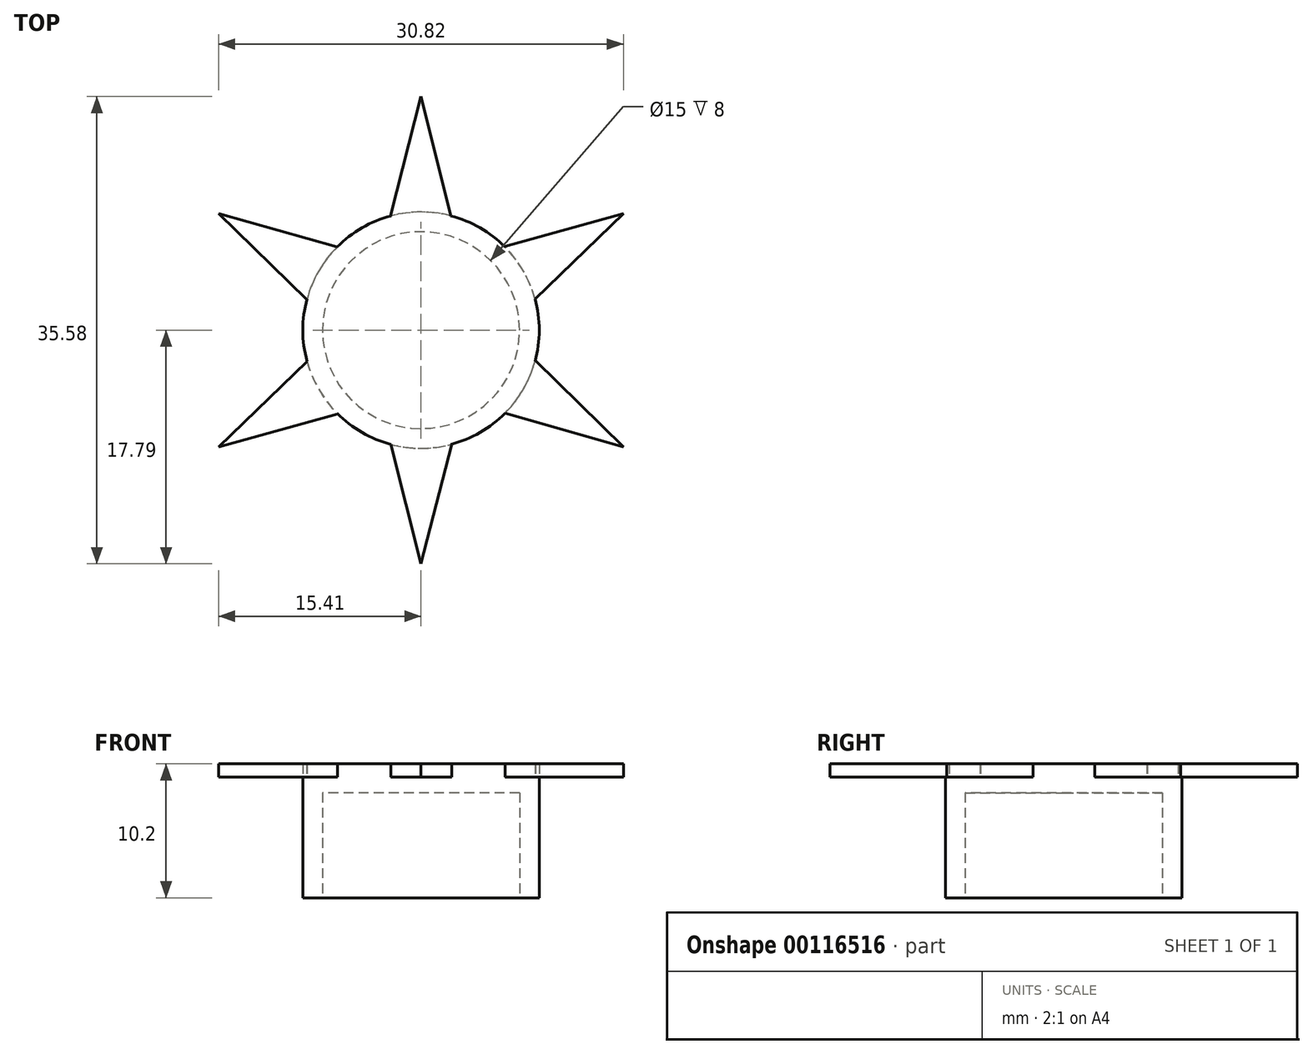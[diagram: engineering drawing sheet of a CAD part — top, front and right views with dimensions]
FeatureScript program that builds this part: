
annotation { "Feature Type Name" : "Feature", "Feature Type Description" : "" }
export const myFeature = defineFeature(function(context is Context, id is Id, definition is map)
    precondition{}
    {
        {
            var Q0;
            Q0=qCreatedBy(makeId("Top.planeOp"),FACE);
            var sketch = newSketch(context, id + "F0", { "sketchPlane" : qUnion([Q0])});
            skCircle(sketch, "E0", {"center": v(0, 0) * mm, "radius": 7.5 * mm});
            skCircle(sketch, "E1", {"center": v(0, 0) * mm, "radius": 9 * mm});
            skSolve(sketch);
        }
        {
            var Q0;
            Q0 = qSketchRegion(id + "F0", true);
            extrude(context, id + "F1", {"entities" : qUnion([Q0]), "depth" : 8 * mm});
        }
        {
            var Q0;
            Q0=makeQuery(id+"F1.opExtrude","CAP_FACE",FACE,{"disambiguationData":[OSD([sQuery(id+"F0.wireOp",EDGE,"E0"),sQuery(id+"F0.wireOp",EDGE,"E1")])],"isStart":false});
            var sketch = newSketch(context, id + "F2", { "sketchPlane" : qUnion([Q0])});
            skCircle(sketch, "E2.0", {"center": v(0, 0) * mm, "radius": 9 * mm});
            skSolve(sketch);
        }
        {
            var Q0;
            Q0 = qSketchRegion(id + "F2", true);
            extrude(context, id + "F3", {"entities" : qUnion([Q0]), "operationType" : NewBodyOperationType.ADD, "depth" : 1.2 * mm});
        }
        {
            var Q0;
            Q0=makeQuery(id+"F3.opExtrude","CAP_FACE",FACE,{"disambiguationData":[OSD([sQuery(id+"F2.wireOp",EDGE,"E2.0")])],"isStart":false});
            var sketch = newSketch(context, id + "F4", { "sketchPlane" : qUnion([Q0])});
            skLineSegment(sketch, "E3", {"start": v(-2.34, 8.7) * mm, "end": v(0, 17.8) * mm});
            skLineSegment(sketch, "E4", {"start": v(0, 17.8) * mm, "end": v(2.28, 8.7) * mm});
            skLineSegment(sketch, "E5.1.0", {"start": v(-8.7, 2.33) * mm, "end": v(-15.4, 8.9) * mm});
            skLineSegment(sketch, "E5.1.1", {"start": v(-15.4, 8.9) * mm, "end": v(-6.4, 6.33) * mm});
            skLineSegment(sketch, "E5.2.0", {"start": v(-6.37, -6.38) * mm, "end": v(-15.4, -8.9) * mm});
            skLineSegment(sketch, "E5.2.1", {"start": v(-15.4, -8.9) * mm, "end": v(-8.68, -2.38) * mm});
            skLineSegment(sketch, "E5.3.0", {"start": v(2.34, -8.7) * mm, "end": v(0, -17.8) * mm});
            skLineSegment(sketch, "E5.3.1", {"start": v(0, -17.8) * mm, "end": v(-2.28, -8.7) * mm});
            skLineSegment(sketch, "E5.4.0", {"start": v(8.7, -2.33) * mm, "end": v(15.4, -8.9) * mm});
            skLineSegment(sketch, "E5.4.1", {"start": v(15.4, -8.9) * mm, "end": v(6.4, -6.33) * mm});
            skLineSegment(sketch, "E5.5.0", {"start": v(6.37, 6.38) * mm, "end": v(15.4, 8.9) * mm});
            skLineSegment(sketch, "E5.5.1", {"start": v(15.4, 8.9) * mm, "end": v(8.68, 2.38) * mm});
            skPoint(sketch, "E5.center", {"position": v(0, 0) * mm});
            skLineSegment(sketch, "E6", {"start": v(-2.34, 8.7) * mm, "end": v(2.28, 8.7) * mm});
            skLineSegment(sketch, "E7.1.0", {"start": v(-8.7, 2.33) * mm, "end": v(-6.4, 6.33) * mm});
            skLineSegment(sketch, "E7.2.0", {"start": v(-6.37, -6.38) * mm, "end": v(-8.68, -2.38) * mm});
            skLineSegment(sketch, "E7.3.0", {"start": v(2.34, -8.7) * mm, "end": v(-2.28, -8.7) * mm});
            skLineSegment(sketch, "E7.4.0", {"start": v(8.7, -2.33) * mm, "end": v(6.4, -6.33) * mm});
            skLineSegment(sketch, "E7.5.0", {"start": v(6.37, 6.38) * mm, "end": v(8.68, 2.38) * mm});
            skSolve(sketch);
        }
        {
            var Q0;
            Q0 = qSketchRegion(id + "F4", true);
            var Q1;
            {var subQ1=makeQuery(id+"F3.opExtrude","CAP_EDGE",EDGE,{"disambiguationData":[OSD([sQuery(id+"F2.wireOp",EDGE,"E2.0")])],"isStart":false});var subQ6=sQuery(id+"F4.wireOp",EDGE,"E6");var subQ7=makeQuery(id+"F4.imprint","INTERSECT",VERTEX,{"derivedFrom":[subQ1,subQ6]});Q1=makeQuery(id+"F4.imprint","IMPRINT",FACE,{"disambiguationData":[TD([[makeQuery(id+"F4.imprint","IMPRINT",EDGE,{"disambiguationData":[TD([[subQ7,-1.0]])],"derivedFrom":subQ6}),-1.0]])]});}
            extrude(context, id + "F5", {"entities" : qUnion([Q0, Q1]), "operationType" : NewBodyOperationType.ADD, "depth" : 1 * mm});
        }
    });
